# Revit family: Lighting-Surface-Amerlux-Rook X-Up-Down
name_source: partatom
category: Lighting Fixtures
units: mm (PartAtom-declared; Revit-internal decimal feet)

## family parameters
Cut with Voids When Loaded = No
Host = Face
Light Source = Yes
Part Type = Normal
Room Calculation Point = No
Round Connector Dimension = Use Diameter
Shared = No

## types (1)
- Lighting-Surface-Amerlux-Rook X-Up-Down
    Apparent Load = 0 VA
    Back Plate Height = 5.17 "
    Color Filter = 16777215
    Default Elevation = 48 "
    Description = Wall Mount
    Dimming Lamp Color Temperature Shift = <None>
    Emit Shape Visible in Rendering = No
    Emit from Circle Diameter = 2.5 "
    Fixture Finish = Aluminum Finish
    Height = 7.24 "
    Manufacturer = Amerlux
    Model = Rook X
    Number of Poles = 1
    Photometric Web File = Load File
    Power Factor = 1
    Tilt Angle = -90.00°
    URL = http://www.amerlux.com
    Voltage = 0 V

## geometry (parser evidence)
native form markers: Sweep x3
no freeform markers — native parametric forms only
